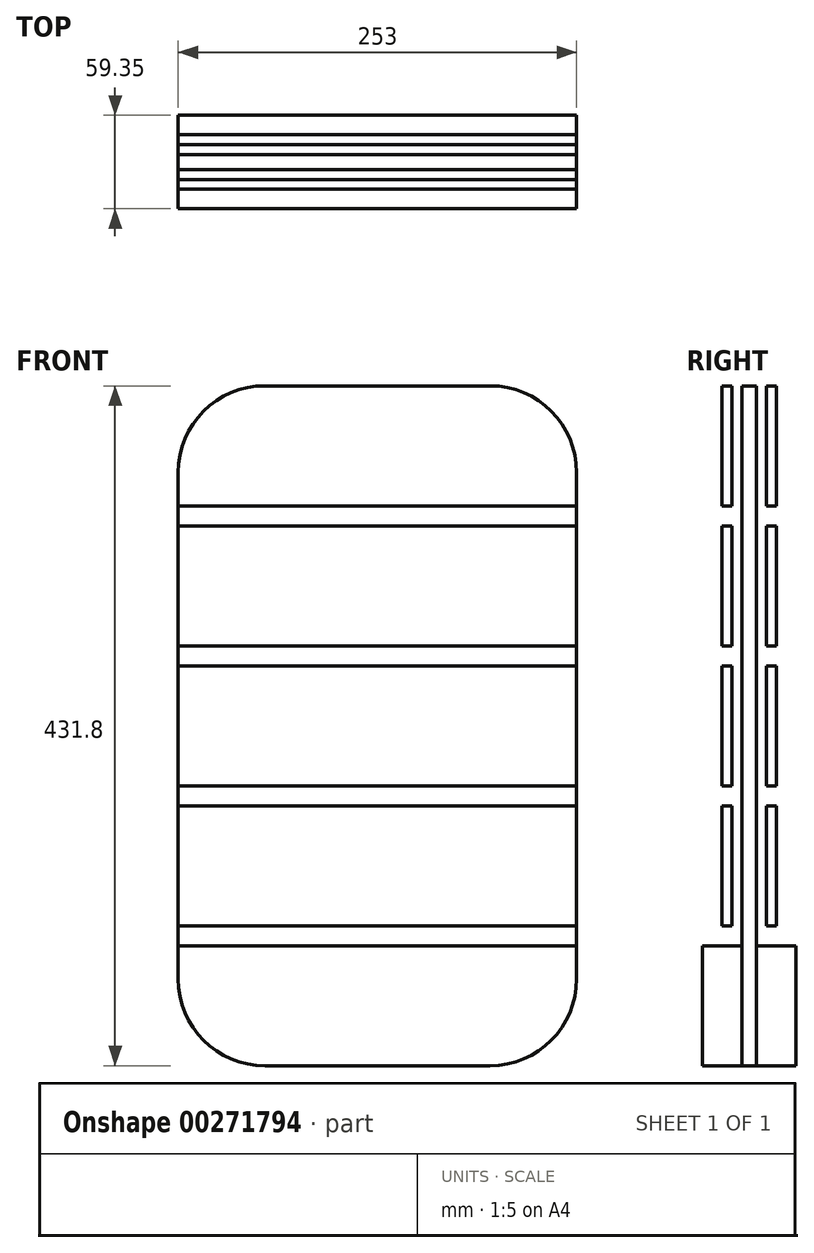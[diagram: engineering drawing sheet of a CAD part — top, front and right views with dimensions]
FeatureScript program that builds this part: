
annotation { "Feature Type Name" : "Feature", "Feature Type Description" : "" }
export const myFeature = defineFeature(function(context is Context, id is Id, definition is map)
    precondition{}
    {
        {
            var Q0;
            Q0=qCreatedBy(makeId("Front.planeOp"),FACE);
            cPlane(context, id + "F0", {"entities" : qUnion([Q0]), "cplaneType" : CPlaneType.OFFSET, "offset" : 6.35 * mm, "oppositeDirection" : true, "width" : 150 * mm, "height" : 150 * mm});
        }
        {
            var Q0;
            Q0=qCreatedBy(makeId("Front.planeOp"),FACE);
            cPlane(context, id + "F1", {"entities" : qUnion([Q0]), "cplaneType" : CPlaneType.OFFSET, "offset" : 22.05 * mm, "oppositeDirection" : true, "width" : 150 * mm, "height" : 150 * mm});
        }
        {
            var Q0;
            Q0=qCreatedBy(makeId("Front.planeOp"),FACE);
            var sketch = newSketch(context, id + "F2", { "sketchPlane" : qUnion([Q0])});
            skLineSegment(sketch, "E0", {"start": v(-126.5, -127.5) * mm, "end": v(-126.5, 194.3) * mm});
            skLineSegment(sketch, "E1", {"start": v(-71.5, 249.3) * mm, "end": v(0, 249.3) * mm});
            skLineSegment(sketch, "E2.0", {"start": v(-126.5, 173.1) * mm, "end": v(0, 173.1) * mm});
            skLineSegment(sketch, "E3.0", {"start": v(-126.5, 160.4) * mm, "end": v(0, 160.4) * mm});
            skLineSegment(sketch, "E4.0", {"start": v(-126.5, 84.2) * mm, "end": v(0, 84.2) * mm});
            skLineSegment(sketch, "E5.0", {"start": v(-126.5, 71.5) * mm, "end": v(0, 71.5) * mm});
            skLineSegment(sketch, "E6.0", {"start": v(-126.5, -4.7) * mm, "end": v(0, -4.7) * mm});
            skLineSegment(sketch, "E7.0", {"start": v(-126.5, -17.4) * mm, "end": v(0, -17.4) * mm});
            skLineSegment(sketch, "E8.0", {"start": v(-126.5, -93.6) * mm, "end": v(0, -93.6) * mm});
            skLineSegment(sketch, "E9.0", {"start": v(-126.5, -106.3) * mm, "end": v(0, -106.3) * mm});
            skLineSegment(sketch, "E10.0", {"start": v(-71.5, -182.5) * mm, "end": v(0, -182.5) * mm});
            skPoint(sketch, "E11.visualSharp", {"position": v(-126.5, -182.5) * mm});
            skArc(sketch, "E11.filletArc", {"start": v(-126.5, -127.5) * mm, "mid": v(-110.4, -166.4) * mm, "end": v(-71.5, -182.5) * mm});
            skPoint(sketch, "E12.orphan", {"position": v(0, 249.3) * mm});
            skPoint(sketch, "E13.visualSharp", {"position": v(-126.5, 249.3) * mm});
            skArc(sketch, "E13.filletArc", {"start": v(-71.5, 249.3) * mm, "mid": v(-110.4, 233.18) * mm, "end": v(-126.5, 194.3) * mm});
            skLineSegment(sketch, "E14", {"start": v(0, 249.3) * mm, "end": v(0, -182.5) * mm});
            skPoint(sketch, "E15.orphan", {"position": v(0, 224.62) * mm});
            skSolve(sketch);
        }
        {
            var Q0;
            Q0=qCreatedBy(makeId("Front.planeOp"),FACE);
            var sketch = newSketch(context, id + "F3", { "sketchPlane" : qUnion([Q0])});
            skLineSegment(sketch, "E16.0", {"start": v(0, 249.3) * mm, "end": v(0, 173.1) * mm});
            skArc(sketch, "E17.0", {"start": v(-126.5, -127.5) * mm, "mid": v(-110.4, -166.4) * mm, "end": v(-71.5, -182.5) * mm, "construction": true});
            skLineSegment(sketch, "E17.1", {"start": v(-71.5, -182.5) * mm, "end": v(0, -182.5) * mm, "construction": true});
            skLineSegment(sketch, "E17.2", {"start": v(-126.5, -127.5) * mm, "end": v(-126.5, -106.3) * mm, "construction": true});
            skLineSegment(sketch, "E17.3", {"start": v(-126.5, -106.3) * mm, "end": v(0, -106.3) * mm, "construction": true});
            skLineSegment(sketch, "E17.4", {"start": v(-126.5, -93.6) * mm, "end": v(0, -93.6) * mm});
            skLineSegment(sketch, "E17.5", {"start": v(-126.5, -17.4) * mm, "end": v(0, -17.4) * mm});
            skLineSegment(sketch, "E17.6", {"start": v(-126.5, -4.7) * mm, "end": v(0, -4.7) * mm});
            skLineSegment(sketch, "E17.7", {"start": v(-126.5, 71.5) * mm, "end": v(0, 71.5) * mm});
            skLineSegment(sketch, "E17.8", {"start": v(-126.5, 84.2) * mm, "end": v(0, 84.2) * mm});
            skLineSegment(sketch, "E17.9", {"start": v(-126.5, 160.4) * mm, "end": v(0, 160.4) * mm});
            skLineSegment(sketch, "E17.10", {"start": v(-126.5, 173.1) * mm, "end": v(0, 173.1) * mm});
            skArc(sketch, "E17.11", {"start": v(-71.5, 249.3) * mm, "mid": v(-110.4, 233.18) * mm, "end": v(-126.5, 194.3) * mm});
            skLineSegment(sketch, "E17.12", {"start": v(-71.5, 249.3) * mm, "end": v(0, 249.3) * mm});
            skLineSegment(sketch, "E18.trimOffspring", {"start": v(-126.5, 173.1) * mm, "end": v(-126.5, 194.3) * mm});
            skLineSegment(sketch, "E19.trimOffspring", {"start": v(0, 160.4) * mm, "end": v(0, 84.2) * mm});
            skLineSegment(sketch, "E20.trimOffspring", {"start": v(0, 71.5) * mm, "end": v(0, -4.7) * mm});
            skLineSegment(sketch, "E21.trimOffspring", {"start": v(-126.5, 84.2) * mm, "end": v(-126.5, 160.4) * mm});
            skLineSegment(sketch, "E22.trimOffspring", {"start": v(-126.5, -4.7) * mm, "end": v(-126.5, 71.5) * mm});
            skLineSegment(sketch, "E23.trimOffspring", {"start": v(0, -17.4) * mm, "end": v(0, -93.6) * mm});
            skLineSegment(sketch, "E24.trimOffspring", {"start": v(0, -106.3) * mm, "end": v(0, -182.5) * mm});
            skLineSegment(sketch, "E25.trimOffspring", {"start": v(-126.5, -93.6) * mm, "end": v(-126.5, -17.4) * mm});
            skLineSegment(sketch, "E26.MirrorCS", {"start": v(71.5, 249.3) * mm, "end": v(0, 249.3) * mm});
            skArc(sketch, "E27.MirrorCS", {"start": v(71.5, 249.3) * mm, "mid": v(110.4, 233.18) * mm, "end": v(126.5, 194.3) * mm});
            skLineSegment(sketch, "E28.MirrorCS", {"start": v(126.5, 173.1) * mm, "end": v(126.5, 194.3) * mm});
            skLineSegment(sketch, "E29.MirrorCS", {"start": v(126.5, 173.1) * mm, "end": v(0, 173.1) * mm});
            skLineSegment(sketch, "E30.MirrorCS", {"start": v(126.5, 84.2) * mm, "end": v(126.5, 160.4) * mm});
            skLineSegment(sketch, "E31.MirrorCS", {"start": v(126.5, 160.4) * mm, "end": v(0, 160.4) * mm});
            skLineSegment(sketch, "E32.MirrorCS", {"start": v(126.5, 84.2) * mm, "end": v(0, 84.2) * mm});
            skLineSegment(sketch, "E33.MirrorCS", {"start": v(126.5, 71.5) * mm, "end": v(0, 71.5) * mm});
            skLineSegment(sketch, "E34.MirrorCS", {"start": v(126.5, -4.7) * mm, "end": v(126.5, 71.5) * mm});
            skLineSegment(sketch, "E35.MirrorCS", {"start": v(126.5, -4.7) * mm, "end": v(0, -4.7) * mm});
            skLineSegment(sketch, "E36.MirrorCS", {"start": v(126.5, -17.4) * mm, "end": v(0, -17.4) * mm});
            skLineSegment(sketch, "E37.MirrorCS", {"start": v(126.5, -93.6) * mm, "end": v(126.5, -17.4) * mm});
            skLineSegment(sketch, "E38.MirrorCS", {"start": v(126.5, -93.6) * mm, "end": v(0, -93.6) * mm});
            skLineSegment(sketch, "E39.MirrorCS", {"start": v(126.5, -106.3) * mm, "end": v(0, -106.3) * mm, "construction": true});
            skLineSegment(sketch, "E40.MirrorCS", {"start": v(126.5, -127.5) * mm, "end": v(126.5, -106.3) * mm, "construction": true});
            skArc(sketch, "E41.MirrorCS", {"start": v(126.5, -127.5) * mm, "mid": v(110.4, -166.4) * mm, "end": v(71.5, -182.5) * mm, "construction": true});
            skLineSegment(sketch, "E42.MirrorCS", {"start": v(71.5, -182.5) * mm, "end": v(0, -182.5) * mm, "construction": true});
            skSolve(sketch);
        }
        {
            var Q0;
            Q0 = qSketchRegion(id + "F3", true);
            extrude(context, id + "F4", {"entities" : qUnion([Q0]), "depth" : 6.3 * mm});
        }
        {
            var Q0;
            Q0=qCreatedBy(id+"F0.planeOp",FACE);
            var sketch = newSketch(context, id + "F5", { "sketchPlane" : qUnion([Q0])});
            skArc(sketch, "E43.0", {"start": v(-71.5, 249.3) * mm, "mid": v(-110.4, 233.18) * mm, "end": v(-126.5, 194.3) * mm});
            skLineSegment(sketch, "E44.0", {"start": v(-126.5, -93.6) * mm, "end": v(-126.5, 194.3) * mm});
            skLineSegment(sketch, "E45.0", {"start": v(0, 249.3) * mm, "end": v(0, -182.5) * mm});
            skLineSegment(sketch, "E46.0", {"start": v(-71.5, 249.3) * mm, "end": v(0, 249.3) * mm});
            skArc(sketch, "E47.MirrorCS", {"start": v(71.5, 249.3) * mm, "mid": v(110.4, 233.18) * mm, "end": v(126.5, 194.3) * mm});
            skLineSegment(sketch, "E48.MirrorCS", {"start": v(126.5, -93.6) * mm, "end": v(126.5, 194.3) * mm});
            skLineSegment(sketch, "E49.MirrorCS", {"start": v(71.5, 249.3) * mm, "end": v(0, 249.3) * mm});
            skLineSegment(sketch, "E50.0", {"start": v(-126.5, -93.6) * mm, "end": v(126.5, -93.6) * mm});
            skPoint(sketch, "E51.orphan", {"position": v(126.5, -127.5) * mm});
            skPoint(sketch, "E52.orphan", {"position": v(-126.5, -127.5) * mm});
            skLineSegment(sketch, "E53.bottom", {"start": v(126.5, -93.6) * mm, "end": v(-126.5, -93.6) * mm});
            skLineSegment(sketch, "E53.top", {"start": v(126.5, -106.3) * mm, "end": v(-126.5, -106.3) * mm});
            skLineSegment(sketch, "E53.left", {"start": v(126.5, -93.6) * mm, "end": v(126.5, -106.3) * mm});
            skLineSegment(sketch, "E53.right", {"start": v(-126.5, -93.6) * mm, "end": v(-126.5, -106.3) * mm});
            skArc(sketch, "E54.0", {"start": v(-126.5, -127.5) * mm, "mid": v(-110.4, -166.4) * mm, "end": v(-71.5, -182.5) * mm});
            skLineSegment(sketch, "E54.1", {"start": v(-126.5, -127.5) * mm, "end": v(-126.5, 194.3) * mm});
            skLineSegment(sketch, "E54.2", {"start": v(-71.5, -182.5) * mm, "end": v(0, -182.5) * mm});
            skPoint(sketch, "E54.3", {"position": v(-35.75, -182.5) * mm});
            skLineSegment(sketch, "E55.MirrorCS", {"start": v(71.5, -182.5) * mm, "end": v(0, -182.5) * mm});
            skArc(sketch, "E56.MirrorCS", {"start": v(126.5, -127.5) * mm, "mid": v(110.4, -166.4) * mm, "end": v(71.5, -182.5) * mm});
            skLineSegment(sketch, "E57.MirrorCS", {"start": v(126.5, -127.5) * mm, "end": v(126.5, 194.3) * mm});
            skSolve(sketch);
        }
        {
            var Q0;
            Q0 = qSketchRegion(id + "F5", true);
            extrude(context, id + "F6", {"entities" : qUnion([Q0]), "oppositeDirection" : true, "depth" : 9.35 * mm});
        }
        {
            var Q0;
            Q0=qCreatedBy(id+"F1.planeOp",FACE);
            var sketch = newSketch(context, id + "F7", { "sketchPlane" : qUnion([Q0])});
            skLineSegment(sketch, "E58.0.0", {"start": v(71.5, 249.3) * mm, "end": v(-71.5, 249.3) * mm});
            skArc(sketch, "E58.0.1", {"start": v(-71.5, 249.3) * mm, "mid": v(-110.4, 233.18) * mm, "end": v(-126.5, 194.3) * mm});
            skLineSegment(sketch, "E58.0.2", {"start": v(-126.5, 194.3) * mm, "end": v(-126.5, 173.1) * mm});
            skLineSegment(sketch, "E58.0.3", {"start": v(-126.5, 173.1) * mm, "end": v(126.5, 173.1) * mm});
            skLineSegment(sketch, "E58.0.4", {"start": v(126.5, 173.1) * mm, "end": v(126.5, 194.3) * mm});
            skArc(sketch, "E58.0.5", {"start": v(126.5, 194.3) * mm, "mid": v(110.4, 233.18) * mm, "end": v(71.5, 249.3) * mm});
            skLineSegment(sketch, "E59.0.0", {"start": v(126.5, 160.4) * mm, "end": v(-126.5, 160.4) * mm});
            skLineSegment(sketch, "E59.0.1", {"start": v(-126.5, 160.4) * mm, "end": v(-126.5, 84.2) * mm});
            skLineSegment(sketch, "E59.0.2", {"start": v(-126.5, 84.2) * mm, "end": v(126.5, 84.2) * mm});
            skLineSegment(sketch, "E59.0.3", {"start": v(126.5, 84.2) * mm, "end": v(126.5, 160.4) * mm});
            skLineSegment(sketch, "E60.0.0", {"start": v(126.5, 71.5) * mm, "end": v(-126.5, 71.5) * mm});
            skLineSegment(sketch, "E60.0.1", {"start": v(-126.5, 71.5) * mm, "end": v(-126.5, -4.7) * mm});
            skLineSegment(sketch, "E60.0.2", {"start": v(-126.5, -4.7) * mm, "end": v(126.5, -4.7) * mm});
            skLineSegment(sketch, "E60.0.3", {"start": v(126.5, -4.7) * mm, "end": v(126.5, 71.5) * mm});
            skLineSegment(sketch, "E61.0.0", {"start": v(126.5, -17.4) * mm, "end": v(-126.5, -17.4) * mm});
            skLineSegment(sketch, "E61.0.1", {"start": v(-126.5, -17.4) * mm, "end": v(-126.5, -93.6) * mm});
            skLineSegment(sketch, "E61.0.2", {"start": v(-126.5, -93.6) * mm, "end": v(126.5, -93.6) * mm});
            skLineSegment(sketch, "E61.0.3", {"start": v(126.5, -93.6) * mm, "end": v(126.5, -17.4) * mm});
            skSolve(sketch);
        }
        {
            var Q0;
            Q0 = qSketchRegion(id + "F7", true);
            extrude(context, id + "F8", {"entities" : qUnion([Q0]), "oppositeDirection" : true, "depth" : 6.35 * mm});
        }
        {
            var Q0;
            Q0=makeQuery(id+"F6.opExtrude","CAP_FACE",FACE,{"disambiguationData":[OSD([sQuery(id+"F5.wireOp",EDGE,"E43.0"),sQuery(id+"F5.wireOp",EDGE,"E44.0"),sQuery(id+"F5.wireOp",EDGE,"E46.0"),sQuery(id+"F5.wireOp",EDGE,"E47.MirrorCS"),sQuery(id+"F5.wireOp",EDGE,"E48.MirrorCS"),sQuery(id+"F5.wireOp",EDGE,"E49.MirrorCS"),sQuery(id+"F5.wireOp",EDGE,"E53.top"),sQuery(id+"F5.wireOp",EDGE,"E53.left"),sQuery(id+"F5.wireOp",EDGE,"E53.right")])],"isStart":true});
            var sketch = newSketch(context, id + "F9", { "sketchPlane" : qUnion([Q0])});
            skArc(sketch, "E62.0", {"start": v(-126.5, -127.5) * mm, "mid": v(-110.4, -166.4) * mm, "end": v(-71.5, -182.5) * mm});
            skLineSegment(sketch, "E62.1", {"start": v(-126.5, -106.3) * mm, "end": v(0, -106.3) * mm});
            skLineSegment(sketch, "E62.2", {"start": v(-126.5, -127.5) * mm, "end": v(-126.5, -106.3) * mm});
            skLineSegment(sketch, "E62.3", {"start": v(0, -106.3) * mm, "end": v(0, -182.5) * mm});
            skLineSegment(sketch, "E62.4", {"start": v(-71.5, -182.5) * mm, "end": v(0, -182.5) * mm});
            skPoint(sketch, "E63.orphan", {"position": v(-126.5, 194.3) * mm});
            skPoint(sketch, "E64.orphan", {"position": v(0, 249.3) * mm});
            skLineSegment(sketch, "E65.MirrorCS", {"start": v(71.5, -182.5) * mm, "end": v(0, -182.5) * mm});
            skArc(sketch, "E66.MirrorCS", {"start": v(126.5, -127.5) * mm, "mid": v(110.4, -166.4) * mm, "end": v(71.5, -182.5) * mm});
            skLineSegment(sketch, "E67.MirrorCS", {"start": v(126.5, -127.5) * mm, "end": v(126.5, -106.3) * mm});
            skLineSegment(sketch, "E68.MirrorCS", {"start": v(126.5, -106.3) * mm, "end": v(0, -106.3) * mm});
            skSolve(sketch);
        }
        {
            var Q0;
            Q0 = qSketchRegion(id + "F9", true);
            extrude(context, id + "F10", {"entities" : qUnion([Q0]), "depth" : 25 * mm});
        }
        {
            var Q0;
            Q0=makeQuery(id+"F6.opExtrude","CAP_FACE",FACE,{"disambiguationData":[OSD([sQuery(id+"F5.wireOp",EDGE,"E43.0"),sQuery(id+"F5.wireOp",EDGE,"E44.0"),sQuery(id+"F5.wireOp",EDGE,"E46.0"),sQuery(id+"F5.wireOp",EDGE,"E47.MirrorCS"),sQuery(id+"F5.wireOp",EDGE,"E48.MirrorCS"),sQuery(id+"F5.wireOp",EDGE,"E49.MirrorCS"),sQuery(id+"F5.wireOp",EDGE,"E53.top"),sQuery(id+"F5.wireOp",EDGE,"E53.left"),sQuery(id+"F5.wireOp",EDGE,"E53.right")])],"isStart":false});
            var sketch = newSketch(context, id + "F11", { "sketchPlane" : qUnion([Q0])});
            skArc(sketch, "E69.0", {"start": v(-126.5, -127.5) * mm, "mid": v(-110.4, -166.4) * mm, "end": v(-71.5, -182.5) * mm});
            skLineSegment(sketch, "E69.1", {"start": v(-126.5, -127.5) * mm, "end": v(-126.5, -106.3) * mm});
            skLineSegment(sketch, "E69.2", {"start": v(71.5, -182.5) * mm, "end": v(-71.5, -182.5) * mm});
            skArc(sketch, "E69.3", {"start": v(126.5, -127.5) * mm, "mid": v(110.4, -166.4) * mm, "end": v(71.5, -182.5) * mm});
            skLineSegment(sketch, "E69.4", {"start": v(126.5, -127.5) * mm, "end": v(126.5, -106.3) * mm});
            skLineSegment(sketch, "E69.5", {"start": v(-126.5, -106.3) * mm, "end": v(126.5, -106.3) * mm});
            skSolve(sketch);
        }
        {
            var Q0;
            Q0 = qSketchRegion(id + "F11", true);
            extrude(context, id + "F12", {"entities" : qUnion([Q0]), "depth" : 25 * mm});
        }
    });
